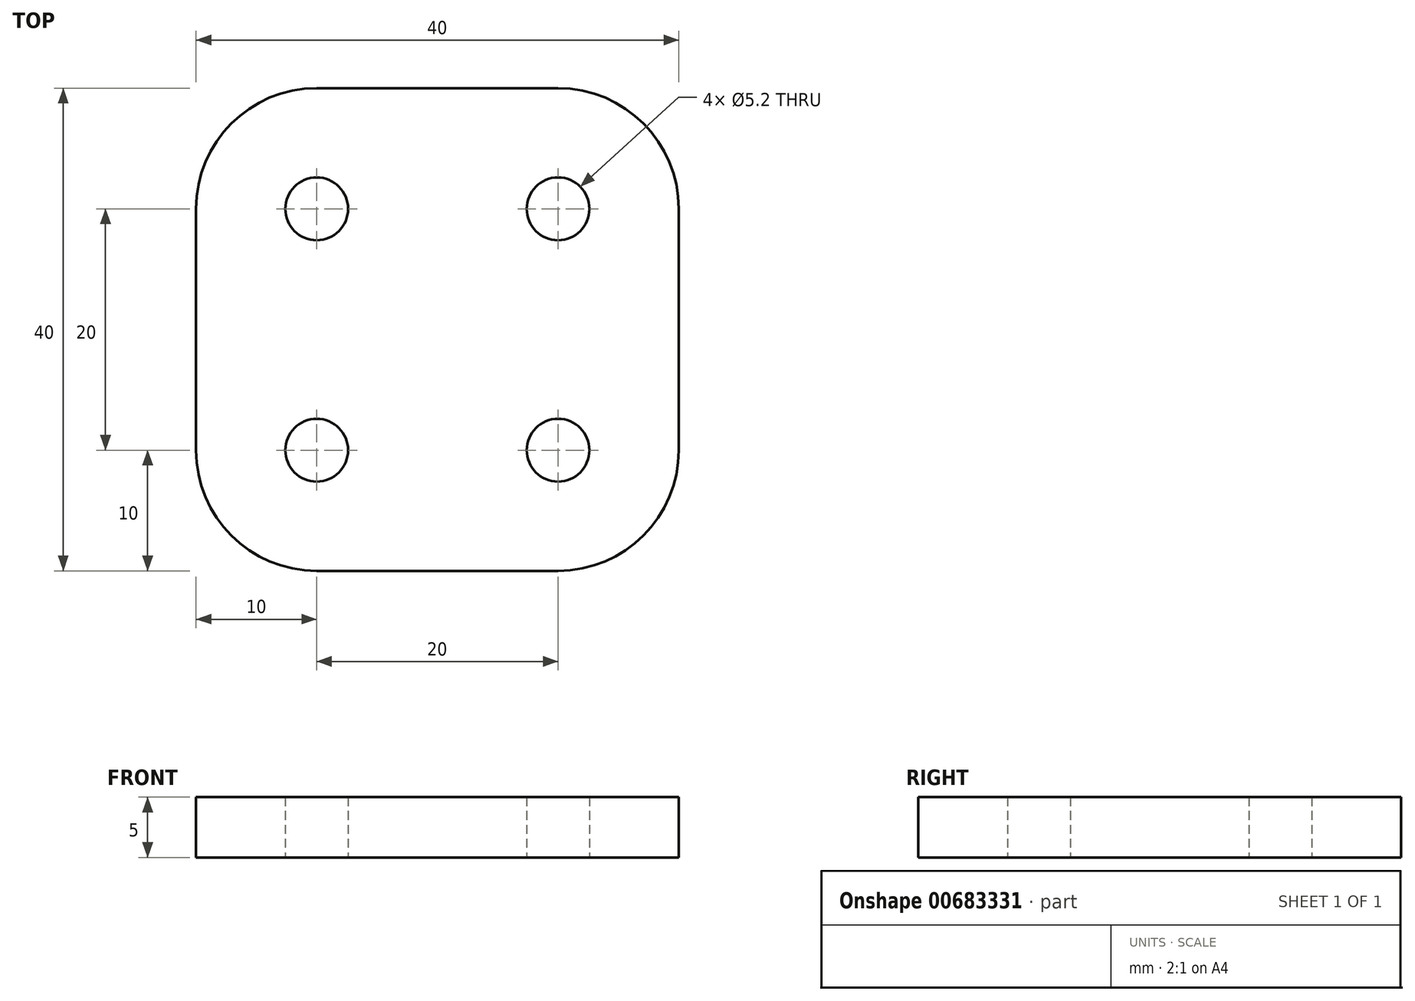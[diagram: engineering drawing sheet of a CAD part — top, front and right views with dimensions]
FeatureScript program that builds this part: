
annotation { "Feature Type Name" : "Feature", "Feature Type Description" : "" }
export const myFeature = defineFeature(function(context is Context, id is Id, definition is map)
    precondition{}
    {
        {
            var Q0;
            Q0=qCreatedBy(makeId("Top.planeOp"),FACE);
            var sketch = newSketch(context, id + "F0", { "sketchPlane" : qUnion([Q0])});
            skLineSegment(sketch, "E0.bottom", {"start": v(20, 20) * mm, "end": v(-20, 20) * mm});
            skLineSegment(sketch, "E0.top", {"start": v(20, -20) * mm, "end": v(-20, -20) * mm});
            skLineSegment(sketch, "E0.left", {"start": v(20, 20) * mm, "end": v(20, -20) * mm});
            skLineSegment(sketch, "E0.right", {"start": v(-20, 20) * mm, "end": v(-20, -20) * mm});
            skPoint(sketch, "E0.middle", {"position": v(0, 0) * mm});
            skLineSegment(sketch, "E1", {"start": v(0, 0) * mm, "end": v(20, 0) * mm, "construction": true});
            skLineSegment(sketch, "E2", {"start": v(20, 0) * mm, "end": v(-20, 0) * mm, "construction": true});
            skLineSegment(sketch, "E3", {"start": v(20, 0) * mm, "end": v(20, 20) * mm, "construction": true});
            skLineSegment(sketch, "E4", {"start": v(20, 10) * mm, "end": v(-20, 10) * mm, "construction": true});
            skLineSegment(sketch, "E5", {"start": v(-20, 0) * mm, "end": v(-20, -20) * mm, "construction": true});
            skLineSegment(sketch, "E6", {"start": v(-20, -10) * mm, "end": v(20, -10) * mm, "construction": true});
            skLineSegment(sketch, "E7", {"start": v(0, 0) * mm, "end": v(10, 0) * mm});
            skLineSegment(sketch, "E8", {"start": v(10, 0) * mm, "end": v(10, 20) * mm});
            skLineSegment(sketch, "E9", {"start": v(10, 20) * mm, "end": v(10, -20) * mm, "construction": true});
            skLineSegment(sketch, "E10", {"start": v(0, 0) * mm, "end": v(-20, 0) * mm, "construction": true});
            skLineSegment(sketch, "E11", {"start": v(-10, 0) * mm, "end": v(-10, 20) * mm, "construction": true});
            skLineSegment(sketch, "E12", {"start": v(-10, 20) * mm, "end": v(-10, -20) * mm, "construction": true});
            skCircle(sketch, "E13", {"center": v(-10, 10) * mm, "radius": 2.6 * mm});
            skCircle(sketch, "E14", {"center": v(10, 10) * mm, "radius": 2.6 * mm});
            skCircle(sketch, "E15", {"center": v(10, -10) * mm, "radius": 2.6 * mm});
            skCircle(sketch, "E16", {"center": v(-10, -10) * mm, "radius": 2.6 * mm});
            skSolve(sketch);
        }
        {
            var Q0;
            Q0 = qSketchRegion(id + "F0", true);
            extrude(context, id + "F1", {"entities" : qUnion([Q0]), "depth" : 5 * mm, "offsetDistance" : 25 * mm});
        }
        {
            var Q0;
            Q0=makeQuery(id+"F1.opExtrude","SWEPT_EDGE",EDGE,{"disambiguationData":[OSD([sQuery(id+"F0.wireOp",EDGE,"E0.top"),sQuery(id+"F0.wireOp",EDGE,"E0.left")])]});
            var Q1;
            Q1=makeQuery(id+"F1.opExtrude","SWEPT_EDGE",EDGE,{"disambiguationData":[OSD([sQuery(id+"F0.wireOp",EDGE,"E0.bottom"),sQuery(id+"F0.wireOp",EDGE,"E0.left")])]});
            var Q2;
            Q2=makeQuery(id+"F1.opExtrude","SWEPT_EDGE",EDGE,{"disambiguationData":[OSD([sQuery(id+"F0.wireOp",EDGE,"E0.top"),sQuery(id+"F0.wireOp",EDGE,"E0.right")])]});
            var Q3;
            Q3=makeQuery(id+"F1.opExtrude","SWEPT_EDGE",EDGE,{"disambiguationData":[OSD([sQuery(id+"F0.wireOp",EDGE,"E0.bottom"),sQuery(id+"F0.wireOp",EDGE,"E0.right")])]});
            fillet(context, id + "F2", {"entities" : qUnion([Q0, Q1, Q2, Q3]), "radius" : 10 * mm, "tangentPropagation" : true, "allowEdgeOverflow" : false});
        }
    });
